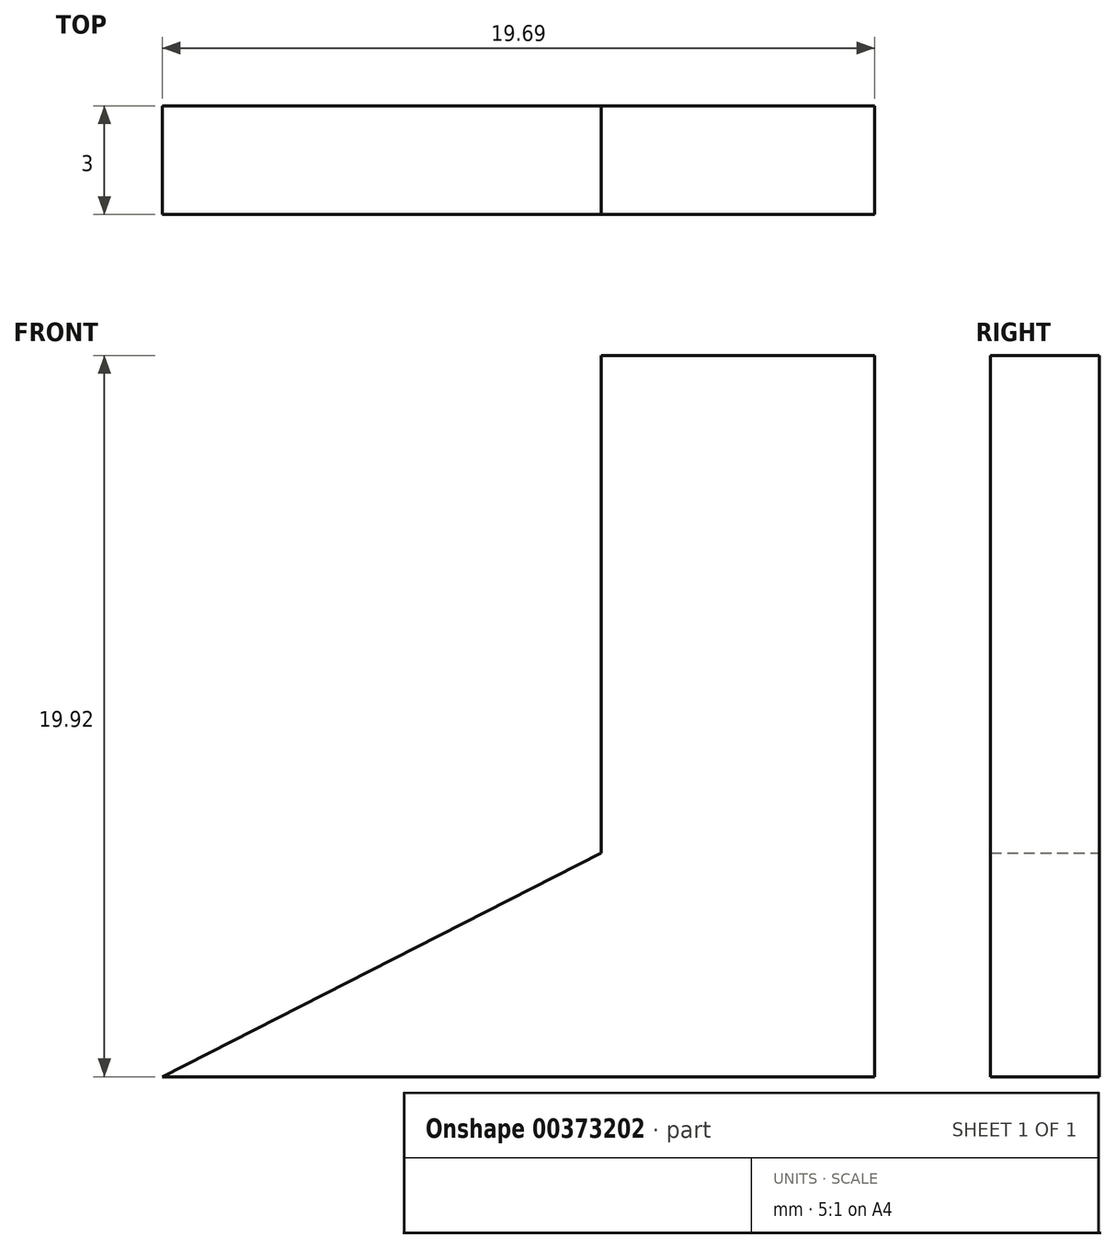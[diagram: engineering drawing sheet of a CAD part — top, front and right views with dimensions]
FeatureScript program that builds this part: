
annotation { "Feature Type Name" : "Feature", "Feature Type Description" : "" }
export const myFeature = defineFeature(function(context is Context, id is Id, definition is map)
    precondition{}
    {
        {
            var Q0;
            Q0=qCreatedBy(makeId("Front.planeOp"),FACE);
            var sketch = newSketch(context, id + "F0", { "sketchPlane" : qUnion([Q0])});
            skLineSegment(sketch, "E0", {"start": v(0, 0) * mm, "end": v(0, 19.92) * mm});
            skLineSegment(sketch, "E1", {"start": v(0, 0) * mm, "end": v(-19.69, 0) * mm});
            skLineSegment(sketch, "E2", {"start": v(-19.69, 0) * mm, "end": v(-7.55, 6.18) * mm});
            skLineSegment(sketch, "E3", {"start": v(0, 19.92) * mm, "end": v(-7.55, 19.92) * mm});
            skLineSegment(sketch, "E4", {"start": v(-7.55, 19.92) * mm, "end": v(-7.55, 6.18) * mm});
            skSolve(sketch);
        }
        {
            var Q0;
            Q0 = qSketchRegion(id + "F0", true);
            extrude(context, id + "F1", {"entities" : qUnion([Q0]), "depth" : 3 * mm});
        }
    });
